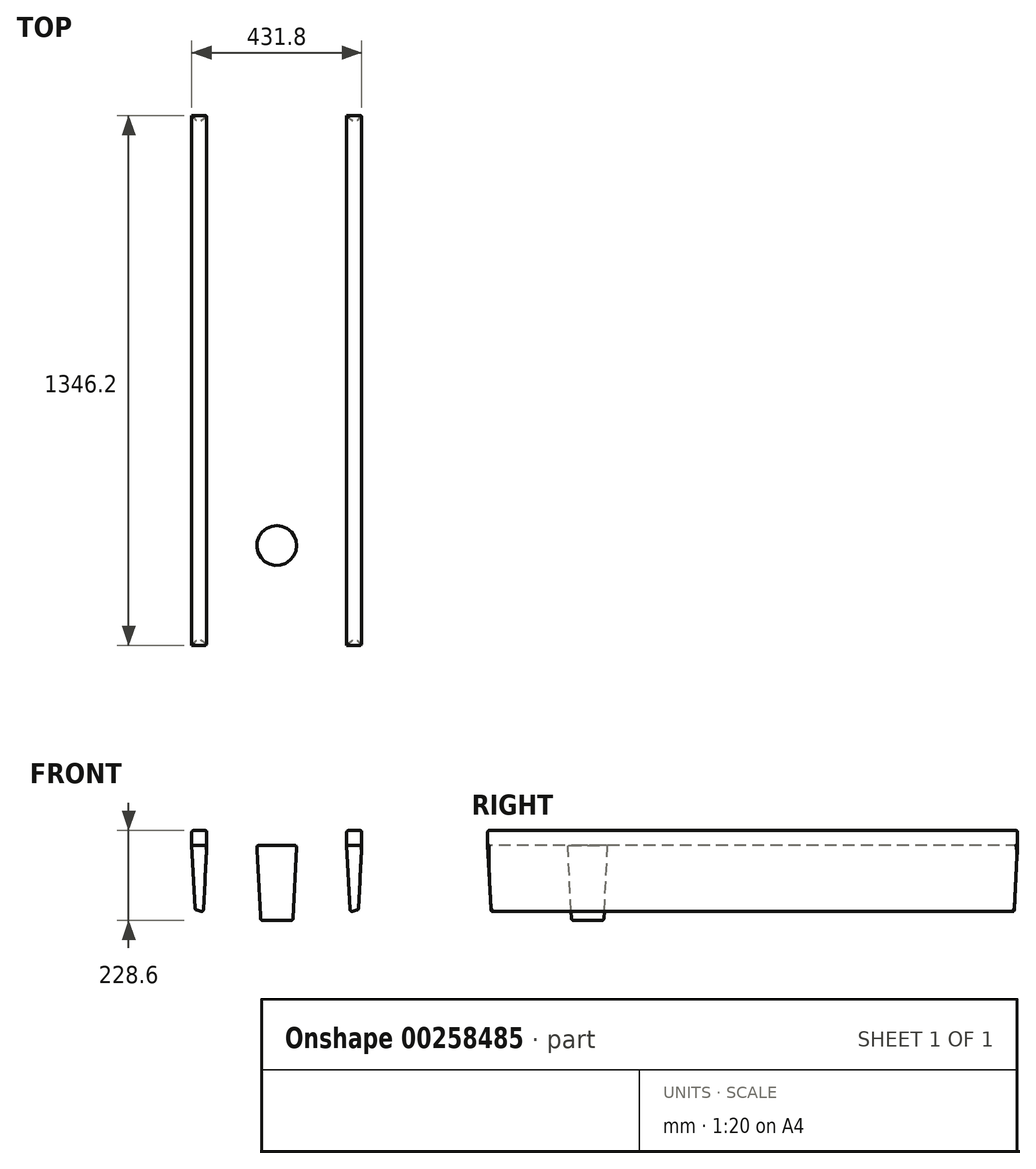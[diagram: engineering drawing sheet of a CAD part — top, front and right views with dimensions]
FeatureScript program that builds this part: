
annotation { "Feature Type Name" : "Feature", "Feature Type Description" : "" }
export const myFeature = defineFeature(function(context is Context, id is Id, definition is map)
    precondition{}
    {
        {
            var Q0;
            Q0=qCreatedBy(makeId("Top.planeOp"),FACE);
            var sketch = newSketch(context, id + "F0", { "sketchPlane" : qUnion([Q0])});
            skLineSegment(sketch, "E0.bottom", {"start": v(317.5, -825.5) * mm, "end": v(-317.5, -825.5) * mm});
            skLineSegment(sketch, "E0.top", {"start": v(317.5, 825.5) * mm, "end": v(-317.5, 825.5) * mm});
            skLineSegment(sketch, "E0.left", {"start": v(317.5, -825.5) * mm, "end": v(317.5, 825.5) * mm});
            skLineSegment(sketch, "E0.right", {"start": v(-317.5, -825.5) * mm, "end": v(-317.5, 825.5) * mm});
            skPoint(sketch, "E0.middle", {"position": v(0, 0) * mm});
            skSolve(sketch);
        }
        {
            var Q0;
            Q0=makeQuery(id+"F0.imprint","IMPRINT",FACE,{"disambiguationData":[TD([[makeQuery(id+"F0.imprint","IMPRINT",EDGE,{"derivedFrom":sQuery(id+"F0.wireOp",EDGE,"E0.bottom")}),-1.0]])]});
            extrude(context, id + "F1", {"entities" : qUnion([Q0]), "depth" : 190.5 * mm});
        }
        {
            var Q0;
            Q0=makeQuery(id+"F1.opExtrude","SWEPT_FACE",FACE,{"disambiguationData":[OSD([sQuery(id+"F0.wireOp",EDGE,"E0.bottom")])]});
            var sketch = newSketch(context, id + "F2", { "sketchPlane" : qUnion([Q0])});
            skLineSegment(sketch, "E1", {"start": v(107.95, 0) * mm, "end": v(317.5, 57.15) * mm});
            skLineSegment(sketch, "E2", {"start": v(0, 0) * mm, "end": v(0, 190.5) * mm, "construction": true});
            skLineSegment(sketch, "E3.MirrorCS", {"start": v(-107.95, 0) * mm, "end": v(-317.5, 57.15) * mm});
            skSolve(sketch);
        }
        {
            var Q0;
            {var subQ0=sQuery(id+"F2.wireOp",EDGE,"E1");Q0=makeQuery(id+"F2.imprint","IMPRINT",FACE,{"disambiguationData":[TD([[makeQuery(id+"F2.imprint","IMPRINT",EDGE,{"derivedFrom":subQ0}),-1.0]])]});}
            var Q1;
            {var subQ0=sQuery(id+"F2.wireOp",EDGE,"E3.MirrorCS");Q1=makeQuery(id+"F2.imprint","IMPRINT",FACE,{"disambiguationData":[TD([[makeQuery(id+"F2.imprint","IMPRINT",EDGE,{"derivedFrom":subQ0}),1.0]])]});}
            extrude(context, id + "F3", {"entities" : qUnion([Q0, Q1]), "operationType" : NewBodyOperationType.REMOVE, "endBound" : BoundingType.THROUGH_ALL, "oppositeDirection" : true, "depth" : 25.4 * mm});
        }
        {
            var Q0;
            Q0=makeQuery(id+"F1.opExtrude","CAP_FACE",FACE,{"disambiguationData":[OSD([sQuery(id+"F0.wireOp",EDGE,"E0.bottom"),sQuery(id+"F0.wireOp",EDGE,"E0.top"),sQuery(id+"F0.wireOp",EDGE,"E0.left"),sQuery(id+"F0.wireOp",EDGE,"E0.right")])],"isStart":false});
            var sketch = newSketch(context, id + "F4", { "sketchPlane" : qUnion([Q0])});
            skLineSegment(sketch, "E4.bottom", {"start": v(-215.9, 673.1) * mm, "end": v(-177.8, 673.1) * mm});
            skLineSegment(sketch, "E4.top", {"start": v(-215.9, -673.1) * mm, "end": v(-177.8, -673.1) * mm});
            skLineSegment(sketch, "E4.left", {"start": v(-215.9, 673.1) * mm, "end": v(-215.9, -673.1) * mm});
            skLineSegment(sketch, "E4.right", {"start": v(-177.8, 673.1) * mm, "end": v(-177.8, -673.1) * mm});
            skLineSegment(sketch, "E5", {"start": v(0, 0) * mm, "end": v(-317.5, 0) * mm, "construction": true});
            skLineSegment(sketch, "E6", {"start": v(0, 0) * mm, "end": v(0, 825.5) * mm, "construction": true});
            skLineSegment(sketch, "E7.MirrorCS", {"start": v(177.8, 673.1) * mm, "end": v(177.8, -673.1) * mm});
            skLineSegment(sketch, "E8.MirrorCS", {"start": v(215.9, 673.1) * mm, "end": v(177.8, 673.1) * mm});
            skLineSegment(sketch, "E9.MirrorCS", {"start": v(215.9, 673.1) * mm, "end": v(215.9, -673.1) * mm});
            skLineSegment(sketch, "E10.MirrorCS", {"start": v(215.9, -673.1) * mm, "end": v(177.8, -673.1) * mm});
            skSolve(sketch);
        }
        {
            var Q0;
            Q0=makeQuery(id+"F4.imprint","IMPRINT",FACE,{"disambiguationData":[TD([[makeQuery(id+"F4.imprint","IMPRINT",EDGE,{"derivedFrom":sQuery(id+"F4.wireOp",EDGE,"E4.bottom")}),-1.0]])]});
            var Q1;
            Q1=makeQuery(id+"F4.imprint","IMPRINT",FACE,{"disambiguationData":[TD([[makeQuery(id+"F4.imprint","IMPRINT",EDGE,{"derivedFrom":sQuery(id+"F4.wireOp",EDGE,"E7.MirrorCS")}),1.0]])]});
            extrude(context, id + "F5", {"entities" : qUnion([Q0, Q1]), "operationType" : NewBodyOperationType.ADD, "depth" : 38.1 * mm});
        }
        {
            var Q0;
            Q0=makeQuery(id+"F5.opExtrude","SWEPT_FACE",FACE,{"disambiguationData":[OSD([sQuery(id+"F4.wireOp",EDGE,"E9.MirrorCS")])]});
            var sketch = newSketch(context, id + "F6", { "sketchPlane" : qUnion([Q0])});
            skLineSegment(sketch, "E11", {"start": v(0, 0) * mm, "end": v(0, 228.6) * mm, "construction": true});
            skLineSegment(sketch, "E12", {"start": v(-673.1, 190.5) * mm, "end": v(-711.2, 228.6) * mm});
            skLineSegment(sketch, "E13.MirrorCS", {"start": v(673.1, 190.5) * mm, "end": v(711.2, 228.6) * mm});
            skSolve(sketch);
        }
        {
            var Q0;
            Q0=makeQuery(id+"F1.opExtrude","CAP_FACE",FACE,{"disambiguationData":[OSD([sQuery(id+"F0.wireOp",EDGE,"E0.bottom"),sQuery(id+"F0.wireOp",EDGE,"E0.top"),sQuery(id+"F0.wireOp",EDGE,"E0.left"),sQuery(id+"F0.wireOp",EDGE,"E0.right")])],"isStart":false});
            var sketch = newSketch(context, id + "F7", { "sketchPlane" : qUnion([Q0])});
            skLineSegment(sketch, "E14", {"start": v(0, 0) * mm, "end": v(317.5, 0) * mm, "construction": true});
            skCircle(sketch, "E15", {"center": v(0, 419.1) * mm, "radius": 50.8 * mm});
            skCircle(sketch, "E16.MirrorC", {"center": v(0, -419.1) * mm, "radius": 50.8 * mm});
            skSolve(sketch);
        }
        {
            var Q0;
            Q0=makeQuery(id+"F7.imprint","IMPRINT",FACE,{"disambiguationData":[TD([[makeQuery(id+"F7.imprint","IMPRINT",EDGE,{"derivedFrom":sQuery(id+"F7.wireOp",EDGE,"E16.MirrorC")}),-1.0]])]});
            var Q1;
            Q1=makeQuery(id+"F7.imprint","IMPRINT",FACE,{"disambiguationData":[TD([[makeQuery(id+"F7.imprint","IMPRINT",EDGE,{"derivedFrom":sQuery(id+"F7.wireOp",EDGE,"E15")}),1.0]])]});
            extrude(context, id + "F8", {"entities" : qUnion([Q0, Q1]), "operationType" : NewBodyOperationType.REMOVE, "endBound" : BoundingType.THROUGH_ALL, "oppositeDirection" : true, "depth" : 25.4 * mm, "hasDraft" : true, "draftAngle" : 3 * degree});
        }
        {
            var Q0;
            Q0=makeQuery(id+"F5.opExtrude","SWEPT_FACE",FACE,{"disambiguationData":[OSD([sQuery(id+"F4.wireOp",EDGE,"E4.right")])]});
            var Q1;
            {var subQ1=sQuery(id+"F4.wireOp",EDGE,"E4.left");Q1=makeQuery(id+"FncI95BMxlU8AJE_1.boolean.opBoolean","COPY",FACE,{"disambiguationData":[TD([makeQuery(id+"F5.opExtrude","SWEPT_FACE",FACE,{"disambiguationData":[OSD([subQ1])]})])],"derivedFrom":makeQuery(id+"FncI95BMxlU8AJE_1.opExtrude","SWEPT_FACE",FACE,{"disambiguationData":[OSD([sQuery(id+"F6.wireOp",EDGE,"E12")])]})});}
            var Q2;
            Q2=makeQuery(id+"F5.opExtrude","CAP_FACE",FACE,{"disambiguationData":[OSD([sQuery(id+"F4.wireOp",EDGE,"E4.bottom"),sQuery(id+"F4.wireOp",EDGE,"E4.top"),sQuery(id+"F4.wireOp",EDGE,"E4.left"),sQuery(id+"F4.wireOp",EDGE,"E4.right")])],"isStart":false});
            var Q3;
            Q3=makeQuery(id+"F5.opExtrude","SWEPT_FACE",FACE,{"disambiguationData":[OSD([sQuery(id+"F4.wireOp",EDGE,"E9.MirrorCS")])]});
            var Q4;
            {var subQ0=sQuery(id+"F4.wireOp",EDGE,"E7.MirrorCS");Q4=makeQuery(id+"FncI95BMxlU8AJE_1.boolean.opBoolean","COPY",FACE,{"disambiguationData":[TD([makeQuery(id+"F5.opExtrude","SWEPT_FACE",FACE,{"disambiguationData":[OSD([subQ0])]})])],"derivedFrom":makeQuery(id+"FncI95BMxlU8AJE_1.opExtrude","SWEPT_FACE",FACE,{"disambiguationData":[OSD([sQuery(id+"F6.wireOp",EDGE,"E12")])]})});}
            var Q5;
            Q5=makeQuery(id+"F5.opExtrude","CAP_FACE",FACE,{"disambiguationData":[OSD([sQuery(id+"F4.wireOp",EDGE,"E7.MirrorCS"),sQuery(id+"F4.wireOp",EDGE,"E8.MirrorCS"),sQuery(id+"F4.wireOp",EDGE,"E9.MirrorCS"),sQuery(id+"F4.wireOp",EDGE,"E10.MirrorCS")])],"isStart":false});
            var Q6;
            Q6=makeQuery(id+"F1.opExtrude","CAP_FACE",FACE,{"disambiguationData":[OSD([sQuery(id+"F0.wireOp",EDGE,"E0.bottom"),sQuery(id+"F0.wireOp",EDGE,"E0.top"),sQuery(id+"F0.wireOp",EDGE,"E0.left"),sQuery(id+"F0.wireOp",EDGE,"E0.right")])],"isStart":false});
            var Q7;
            Q7=makeQuery(id+"F1.opExtrude","SWEPT_FACE",FACE,{"disambiguationData":[OSD([sQuery(id+"F0.wireOp",EDGE,"E0.left")])]});
            var Q8;
            Q8=makeQuery(id+"F1.opExtrude","SWEPT_FACE",FACE,{"disambiguationData":[OSD([sQuery(id+"F0.wireOp",EDGE,"E0.bottom")])]});
            var Q9;
            {var subQ0=sQuery(id+"F4.wireOp",EDGE,"E7.MirrorCS");Q9=makeQuery(id+"FncI95BMxlU8AJE_1.boolean.opBoolean","COPY",FACE,{"disambiguationData":[TD([makeQuery(id+"F5.opExtrude","SWEPT_FACE",FACE,{"disambiguationData":[OSD([subQ0])]})])],"derivedFrom":makeQuery(id+"FncI95BMxlU8AJE_1.opExtrude","SWEPT_FACE",FACE,{"disambiguationData":[OSD([sQuery(id+"F6.wireOp",EDGE,"E13.MirrorCS")])]})});}
            var Q10;
            {var subQ1=sQuery(id+"F4.wireOp",EDGE,"E4.left");Q10=makeQuery(id+"FncI95BMxlU8AJE_1.boolean.opBoolean","COPY",FACE,{"disambiguationData":[TD([makeQuery(id+"F5.opExtrude","SWEPT_FACE",FACE,{"disambiguationData":[OSD([subQ1])]})])],"derivedFrom":makeQuery(id+"FncI95BMxlU8AJE_1.opExtrude","SWEPT_FACE",FACE,{"disambiguationData":[OSD([sQuery(id+"F6.wireOp",EDGE,"E13.MirrorCS")])]})});}
            var Q11;
            Q11=makeQuery(id+"F1.opExtrude","SWEPT_FACE",FACE,{"disambiguationData":[OSD([sQuery(id+"F0.wireOp",EDGE,"E0.top")])]});
            var Q12;
            Q12=makeQuery(id+"F3.boolean.opBoolean","COPY",FACE,{"derivedFrom":makeQuery(id+"F3.opExtrude","SWEPT_FACE",FACE,{"disambiguationData":[OSD([sQuery(id+"F2.wireOp",EDGE,"E3.MirrorCS")])]})});
            var Q13;
            Q13=makeQuery(id+"F1.opExtrude","CAP_FACE",FACE,{"disambiguationData":[OSD([sQuery(id+"F0.wireOp",EDGE,"E0.bottom"),sQuery(id+"F0.wireOp",EDGE,"E0.top"),sQuery(id+"F0.wireOp",EDGE,"E0.left"),sQuery(id+"F0.wireOp",EDGE,"E0.right")])],"isStart":true});
            var Q14;
            Q14=makeQuery(id+"F3.boolean.opBoolean","COPY",FACE,{"derivedFrom":makeQuery(id+"F3.opExtrude","SWEPT_FACE",FACE,{"disambiguationData":[OSD([sQuery(id+"F2.wireOp",EDGE,"E1")])]})});
            fillet(context, id + "F9", {"entities" : qUnion([Q0, Q1, Q2, Q3, Q4, Q5, Q6, Q7, Q8, Q9, Q10, Q11, Q12, Q13, Q14]), "radius" : 4.76 * mm, "tangentPropagation" : true, "allowEdgeOverflow" : false});
        }
    });
